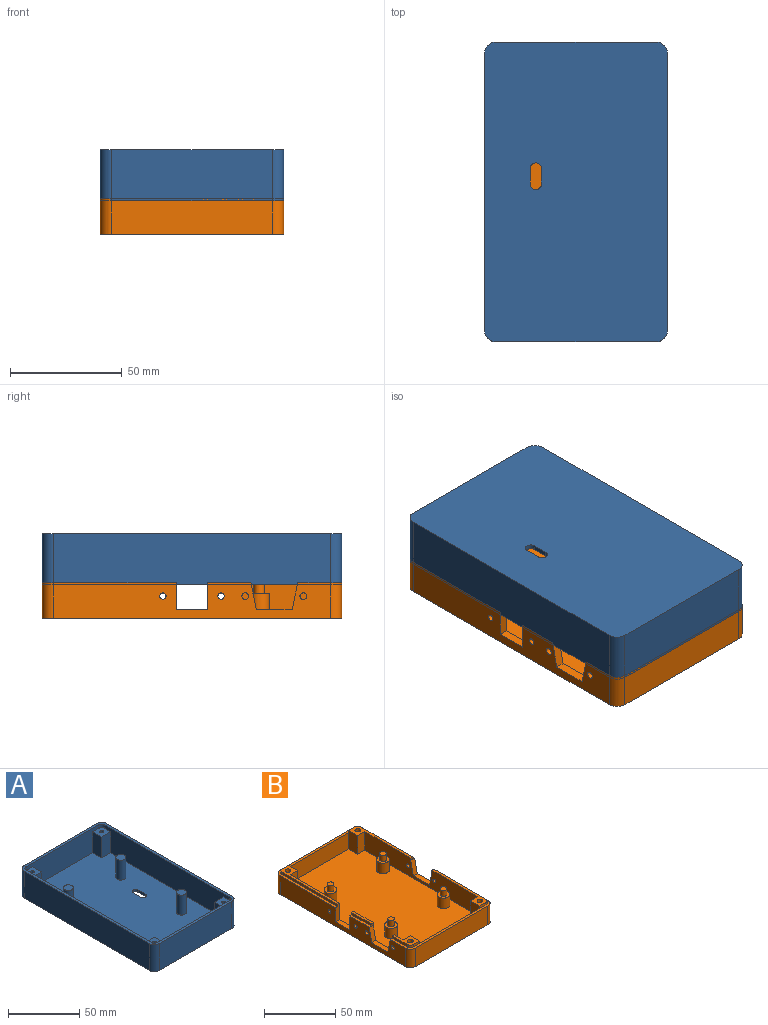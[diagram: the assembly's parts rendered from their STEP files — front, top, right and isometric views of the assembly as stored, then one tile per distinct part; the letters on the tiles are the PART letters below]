
ASSEMBLY  parts=2 mates=1
PART A: 49 faces, bbox 82x134x23 mm
  f0: plane 130x78mm, normal (0,0,1), area 9645.9mm2, adj f2,f3,f14,f18,f19,f21,f23,f25
  f1: plane 134x82mm, normal (0,0,-1), area 10911.9mm2, adj f4,f5,f6,f7,f8,f9,f10,f11
  f2: plane 72x21mm, normal (0,1,0), area 1296mm2, adj f0,f12,f16,f17,f30,f33,f36,f38
  f3: plane 124x21mm, normal (1,0,0), area 2388mm2, adj f0,f12,f15,f16,f25,f28,f31,f33
  f4: cylinder r=5mm len=23mm, axis (0,0,-1), area 180.6mm2, adj f1,f5,f11,f12
  f5: plane 72x23mm, normal (0,1,0), area 1656mm2, adj f1,f4,f6,f12
  f6: cylinder r=5mm len=23mm, axis (0,0,-1), area 180.6mm2, adj f1,f5,f7,f12
  f7: plane 124x23mm, normal (-1,0,0), area 2852mm2, adj f1,f6,f8,f12
  f8: cylinder r=5mm len=23mm, axis (0,0,-1), area 180.6mm2, adj f1,f7,f9,f12
  f9: plane 72x23mm, normal (0,-1,0), area 1656mm2, adj f1,f8,f10,f12
  f10: cylinder r=5mm len=23mm, axis (0,0,-1), area 180.6mm2, adj f1,f9,f11,f12
  f11: plane 124x23mm, normal (1,0,0), area 2852mm2, adj f1,f4,f10,f12
  f12: plane 134x82mm, normal (0,0,1), area 834.3mm2, adj f2,f3,f4,f5,f6,f7,f8,f9
  f13: cylinder r=3mm len=3mm, axis (0,0,-1), area 14.1mm2, adj f12,f14,f18,f43
  f14: plane 72x21mm, normal (0,-1,0), area 1296mm2, adj f0,f12,f13,f15,f26,f28,f40,f43
  f15: cylinder r=3mm len=3mm, axis (0,0,-1), area 14.1mm2, adj f3,f12,f14,f28
  f16: cylinder r=3mm len=3mm, axis (0,0,-1), area 14.1mm2, adj f2,f3,f12,f33
  f17: cylinder r=3mm len=3mm, axis (0,0,-1), area 14.1mm2, adj f2,f12,f18,f38
  f18: plane 124x21mm, normal (-1,0,0), area 2388mm2, adj f0,f12,f13,f17,f35,f38,f41,f43
  f19: cylinder r=3.5mm len=17mm, axis (0,0,-1), area 373.8mm2, adj f0,f20
  f20: plane 7x7mm, normal (0,0,1), area 38.5mm2, adj f19
  f21: cylinder r=3.5mm len=17mm, axis (0,0,-1), area 373.8mm2, adj f0,f22
  f22: plane 7x7mm, normal (0,0,1), area 38.5mm2, adj f21
  f23: cylinder r=3.5mm len=17mm, axis (0,0,-1), area 373.8mm2, adj f0,f24
  f24: plane 7x7mm, normal (0,0,1), area 38.5mm2, adj f23
  f25: plane 18x9mm, normal (0,-1,0), area 162mm2, adj f0,f3,f26,f28
  f26: plane 18x9mm, normal (1,0,0), area 162mm2, adj f0,f14,f25,f28
  f27: cylinder r=1.4mm len=18mm, axis (0,0,-1), area 158.3mm2, adj f28,f29
  f28: plane 9x9mm, normal (0,0,1), area 72.9mm2, adj f3,f14,f15,f25,f26,f27
  f29: plane 2.8x2.8mm, normal (0,0,1), area 6.2mm2, adj f27
  f30: plane 18x9mm, normal (1,0,0), area 162mm2, adj f0,f2,f31,f33
  f31: plane 18x9mm, normal (0,1,0), area 162mm2, adj f0,f3,f30,f33
  f32: cylinder r=1.4mm len=18mm, axis (0,0,-1), area 158.3mm2, adj f33,f34
  f33: plane 9x9mm, normal (0,0,1), area 72.9mm2, adj f2,f3,f16,f30,f31,f32
  f34: plane 2.8x2.8mm, normal (0,0,1), area 6.2mm2, adj f32
  f35: plane 18x9mm, normal (0,1,0), area 162mm2, adj f0,f18,f36,f38
  f36: plane 18x9mm, normal (-1,0,0), area 162mm2, adj f0,f2,f35,f38
  f37: cylinder r=1.4mm len=18mm, axis (0,0,-1), area 158.3mm2, adj f38,f39
  f38: plane 9x9mm, normal (0,0,1), area 72.9mm2, adj f2,f17,f18,f35,f36,f37
  f39: plane 2.8x2.8mm, normal (0,0,1), area 6.2mm2, adj f37
  f40: plane 18x9mm, normal (-1,0,0), area 162mm2, adj f0,f14,f41,f43
  f41: plane 18x9mm, normal (0,-1,0), area 162mm2, adj f0,f18,f40,f43
  f42: cylinder r=1.4mm len=18mm, axis (0,0,-1), area 158.3mm2, adj f43,f44
  f43: plane 9x9mm, normal (0,0,1), area 72.9mm2, adj f13,f14,f18,f40,f41,f42
  f44: plane 2.8x2.8mm, normal (0,0,1), area 6.2mm2, adj f42
  f45: cylinder r=2.5mm len=5mm, axis (0,0,1), area 15.7mm2, adj f0,f1,f46,f48
  f46: plane 7x2mm, normal (1,0,0), area 14mm2, adj f0,f1,f45,f47
  f47: cylinder r=2.5mm len=5mm, axis (0,0,1), area 15.7mm2, adj f0,f1,f46,f48
  f48: plane 7x2mm, normal (-1,0,0), area 14mm2, adj f0,f1,f45,f47
PART B: 94 faces, bbox 82x134x18 mm
  f0: plane 17.67x9mm, normal (0,0,1), area 83.9mm2, adj f7,f50,f51,f53,f54,f55,f73,f78
  f1: plane 19.33x2mm, normal (0,0,1), area 38.7mm2, adj f5,f7,f68,f69
  f2: plane 19.33x2mm, normal (0,0,1), area 38.7mm2, adj f4,f5,f68,f70
  f3: plane 82x60mm, normal (0,0,1), area 382.1mm2, adj f4,f6,f9,f13,f16,f17,f18,f39
  f4: plane 124x16mm, normal (-1,0,0), area 1567.5mm2, adj f2,f3,f10,f18,f19,f22,f66,f67
  f5: plane 19.33x2mm, normal (-1,0,0), area 38.7mm2, adj f1,f2,f68,f69
  f6: plane 55x2mm, normal (-1,0,0), area 110mm2, adj f3,f52,f56,f66
  f7: plane 112x16mm, normal (1,0,0), area 1305.5mm2, adj f0,f1,f15,f54,f56,f57,f66,f67
  f8: plane 54.5x9mm, normal (0,0,1), area 157.5mm2, adj f12,f39,f41,f43,f47,f48,f60,f84
  f9: plane 124x16mm, normal (1,0,0), area 1747.9mm2, adj f3,f10,f16,f21,f22,f61,f62,f63
  f10: plane 82x56.5mm, normal (0,0,1), area 301.5mm2, adj f4,f9,f11,f14,f19,f20,f21,f40
  f11: plane 51.5x2mm, normal (1,0,0), area 103mm2, adj f10,f42,f46,f59
  f12: plane 112x16mm, normal (-1,0,0), area 1513.9mm2, adj f8,f15,f45,f46,f48,f59,f60,f61
  f13: plane 60x14mm, normal (0,-1,0), area 840mm2, adj f3,f15,f47,f58
  f14: plane 60x14mm, normal (0,1,0), area 840mm2, adj f10,f15,f44,f55
  f15: plane 130x74mm, normal (0,0,1), area 9113.5mm2, adj f7,f12,f13,f14,f23,f25,f27,f29
  f16: cylinder r=5mm len=16mm, axis (0,0,-1), area 125.7mm2, adj f3,f9,f17,f22
  f17: plane 72x16mm, normal (0,1,0), area 1152mm2, adj f3,f16,f18,f22
  f18: cylinder r=5mm len=16mm, axis (0,0,-1), area 125.7mm2, adj f3,f4,f17,f22
  f19: cylinder r=5mm len=16mm, axis (0,0,-1), area 125.7mm2, adj f4,f10,f20,f22
  f20: plane 72x16mm, normal (0,-1,0), area 1152mm2, adj f10,f19,f21,f22
  f21: cylinder r=5mm len=16mm, axis (0,0,-1), area 125.7mm2, adj f9,f10,f20,f22
  f22: plane 134x82mm, normal (0,0,-1), area 10966.5mm2, adj f4,f9,f16,f17,f18,f19,f20,f21
  f23: cylinder r=4.5mm len=9mm, axis (0,0,-1), area 254.5mm2, adj f15,f24
  f24: plane 9x9mm, normal (0,0,1), area 45.5mm2, adj f23,f33
  f25: cylinder r=4.5mm len=9mm, axis (0,0,-1), area 254.5mm2, adj f15,f26
  f26: plane 9x9mm, normal (0,0,1), area 45.5mm2, adj f25,f31
  f27: cylinder r=4.5mm len=9mm, axis (0,0,-1), area 254.5mm2, adj f15,f28
  f28: plane 9x9mm, normal (0,0,1), area 45.5mm2, adj f27,f35
  f29: cylinder r=4.5mm len=9mm, axis (0,0,-1), area 254.5mm2, adj f15,f30
  f30: plane 9x9mm, normal (0,0,1), area 45.5mm2, adj f29,f37
  f31: cylinder r=2.4mm len=5mm, axis (0,0,-1), area 75.4mm2, adj f26,f32
  f32: plane 4.8x4.8mm, normal (0,0,1), area 18.1mm2, adj f31
  f33: cylinder r=2.4mm len=5mm, axis (0,0,-1), area 75.4mm2, adj f24,f34
  f34: plane 4.8x4.8mm, normal (0,0,1), area 18.1mm2, adj f33
  f35: cylinder r=2.4mm len=5mm, axis (0,0,-1), area 75.4mm2, adj f28,f36
  f36: plane 4.8x4.8mm, normal (0,0,1), area 18.1mm2, adj f35
  f37: cylinder r=2.4mm len=5mm, axis (0,0,-1), area 75.4mm2, adj f30,f38
  f38: plane 4.8x4.8mm, normal (0,0,1), area 18.1mm2, adj f37
  f39: plane 6x2mm, normal (0,1,0), area 12mm2, adj f3,f8,f43,f47
  f40: plane 6x2mm, normal (0,-1,0), area 12mm2, adj f10,f42,f44,f46
  f41: plane 51.5x2mm, normal (1,0,0), area 103mm2, adj f3,f8,f43,f60
  f42: cylinder r=3mm len=3mm, axis (0,0,-1), area 9.4mm2, adj f10,f11,f40,f46
  f43: cylinder r=3mm len=3mm, axis (0,0,-1), area 9.4mm2, adj f3,f8,f39,f41
  f44: plane 16x9mm, normal (-1,0,0), area 144mm2, adj f14,f15,f40,f45,f46
  f45: plane 16x7mm, normal (0,1,0), area 112mm2, adj f12,f15,f44,f46
  f46: plane 54.5x9mm, normal (0,0,1), area 157.5mm2, adj f11,f12,f40,f42,f44,f45,f59,f80
  f47: plane 16x9mm, normal (-1,0,0), area 144mm2, adj f8,f13,f15,f39,f48
  f48: plane 16x7mm, normal (0,-1,0), area 112mm2, adj f8,f12,f15,f47
  f49: plane 6x2mm, normal (0,1,0), area 12mm2, adj f3,f52,f56,f58
  f50: plane 14.67x2mm, normal (-1,0,0), area 29.3mm2, adj f0,f10,f53,f73
  f51: plane 6x2mm, normal (0,-1,0), area 12mm2, adj f0,f10,f53,f55
  f52: cylinder r=3mm len=3mm, axis (0,0,-1), area 9.4mm2, adj f3,f6,f49,f56
  f53: cylinder r=3mm len=3mm, axis (0,0,-1), area 9.4mm2, adj f0,f10,f50,f51
  f54: plane 16x7mm, normal (0,1,0), area 112mm2, adj f0,f7,f15,f55
  f55: plane 16x9mm, normal (1,0,0), area 144mm2, adj f0,f14,f15,f51,f54
  f56: plane 58x9mm, normal (0,0,1), area 164.5mm2, adj f6,f7,f49,f52,f57,f58,f66,f82
  f57: plane 16x7mm, normal (0,-1,0), area 112mm2, adj f7,f15,f56,f58
  f58: plane 16x9mm, normal (1,0,0), area 144mm2, adj f13,f15,f49,f56,f57
  f59: plane 2x2mm, normal (0,1,0), area 4mm2, adj f11,f12,f46,f61
  f60: plane 2x2mm, normal (0,-1,0), area 4mm2, adj f8,f12,f41,f63
  f61: plane 12x4mm, normal (0,0.98,0.2), area 49mm2, adj f9,f10,f12,f59,f62
  f62: plane 16x4mm, normal (0,0,1), area 64mm2, adj f9,f12,f61,f63
  f63: plane 12x4mm, normal (0,-0.98,0.2), area 49mm2, adj f3,f9,f12,f60,f62
  f64: cylinder r=1.5mm len=4mm, axis (1,0,0), area 37.7mm2, adj f9,f12
  f65: cylinder r=1.5mm len=4mm, axis (1,0,0), area 37.7mm2, adj f9,f12
  f66: plane 14x4mm, normal (0,-1,0), area 52mm2, adj f3,f4,f6,f7,f56,f67
  f67: plane 14x4mm, normal (0,0,1), area 56mm2, adj f4,f7,f66,f68
  f68: plane 14x4mm, normal (0,1,0), area 52mm2, adj f1,f2,f4,f5,f7,f67
  f69: plane 2x2mm, normal (0,-1,0), area 4mm2, adj f1,f5,f7,f70
  f70: plane 12x4mm, normal (0,-0.98,0.2), area 49mm2, adj f2,f4,f7,f69,f71
  f71: plane 16x4mm, normal (0,0,1), area 64mm2, adj f4,f7,f70,f72
  f72: plane 12x4mm, normal (0,0.98,0.2), area 49mm2, adj f4,f7,f10,f71,f73
  f73: plane 2x2mm, normal (0,1,0), area 4mm2, adj f0,f7,f50,f72
  f74: cylinder r=1.5mm len=4mm, axis (-1,0,0), area 37.7mm2, adj f4,f7
  f75: cylinder r=1.5mm len=4mm, axis (-1,0,0), area 37.7mm2, adj f4,f7
  f76: cylinder r=1.4mm len=4mm, axis (-1,0,0), area 35.2mm2, adj f4,f7
  f77: cylinder r=1.4mm len=4mm, axis (-1,0,0), area 35.2mm2, adj f4,f7
  f78: cylinder r=2mm len=13.4mm, axis (0,0,-1), area 168.4mm2, adj f0,f79
  f79: cone r=2mm half-angle=30deg, axis (0,0,-1), area 51.8mm2, adj f78,f92
  f80: cylinder r=2mm len=13.4mm, axis (0,0,-1), area 168.4mm2, adj f46,f81
  f81: cone r=2mm half-angle=30deg, axis (0,0,-1), area 51.8mm2, adj f80,f90
  f82: cylinder r=2mm len=13.4mm, axis (0,0,-1), area 168.4mm2, adj f56,f83
  f83: cone r=2mm half-angle=30deg, axis (0,0,-1), area 51.8mm2, adj f82,f88
  f84: cylinder r=2mm len=13.4mm, axis (0,0,-1), area 168.4mm2, adj f8,f85
  f85: cone r=2mm half-angle=30deg, axis (0,0,-1), area 51.8mm2, adj f84,f86
  f86: cylinder r=3.5mm len=7mm, axis (0,0,1), area 39.6mm2, adj f85,f87
  f87: plane 7x7mm, normal (0,0,1), area 38.5mm2, adj f86
  f88: cylinder r=3.5mm len=7mm, axis (0,0,1), area 39.6mm2, adj f83,f89
  f89: plane 7x7mm, normal (0,0,1), area 38.5mm2, adj f88
  f90: cylinder r=3.5mm len=7mm, axis (0,0,1), area 39.6mm2, adj f81,f91
  f91: plane 7x7mm, normal (0,0,1), area 38.5mm2, adj f90
  f92: cylinder r=3.5mm len=7mm, axis (0,0,1), area 39.6mm2, adj f79,f93
  f93: plane 7x7mm, normal (0,0,1), area 38.5mm2, adj f92
PLACE A rot(axis=(0,1,0),180deg) t=(100,0,38)mm
PLACE B at identity
MATE fastened A.f32 <-> B.f80  axis (0,0,-1) through (34.5,-60.5,18)mm
